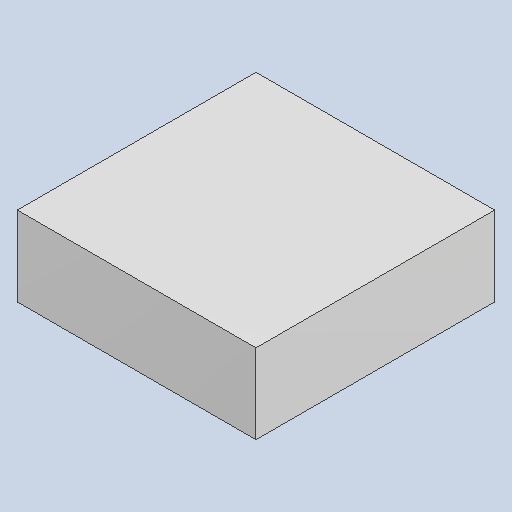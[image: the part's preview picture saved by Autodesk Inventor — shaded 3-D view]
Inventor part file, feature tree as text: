
AUTODESK INVENTOR PART (.ipt)
format: ipt  version: 2023.4 (Build 274418000, 418)  size: 79,872 bytes
history: native  units: mm
features: extrude x1
ambient origin geometry x8: Origin, YZ Plane, XZ Plane, XY Plane, X Axis, Y Axis, Z Axis, Center Point
bodies: Solid1 (feature_tree)
feature tree (1):
  extrude  "Extruded_39"  [1 undecoded]
note: 1 required parameter value undecoded (feature->parameter linkage not recoverable at this tier; creation-order binding heuristic only, values carry confidence <= 0.55)
